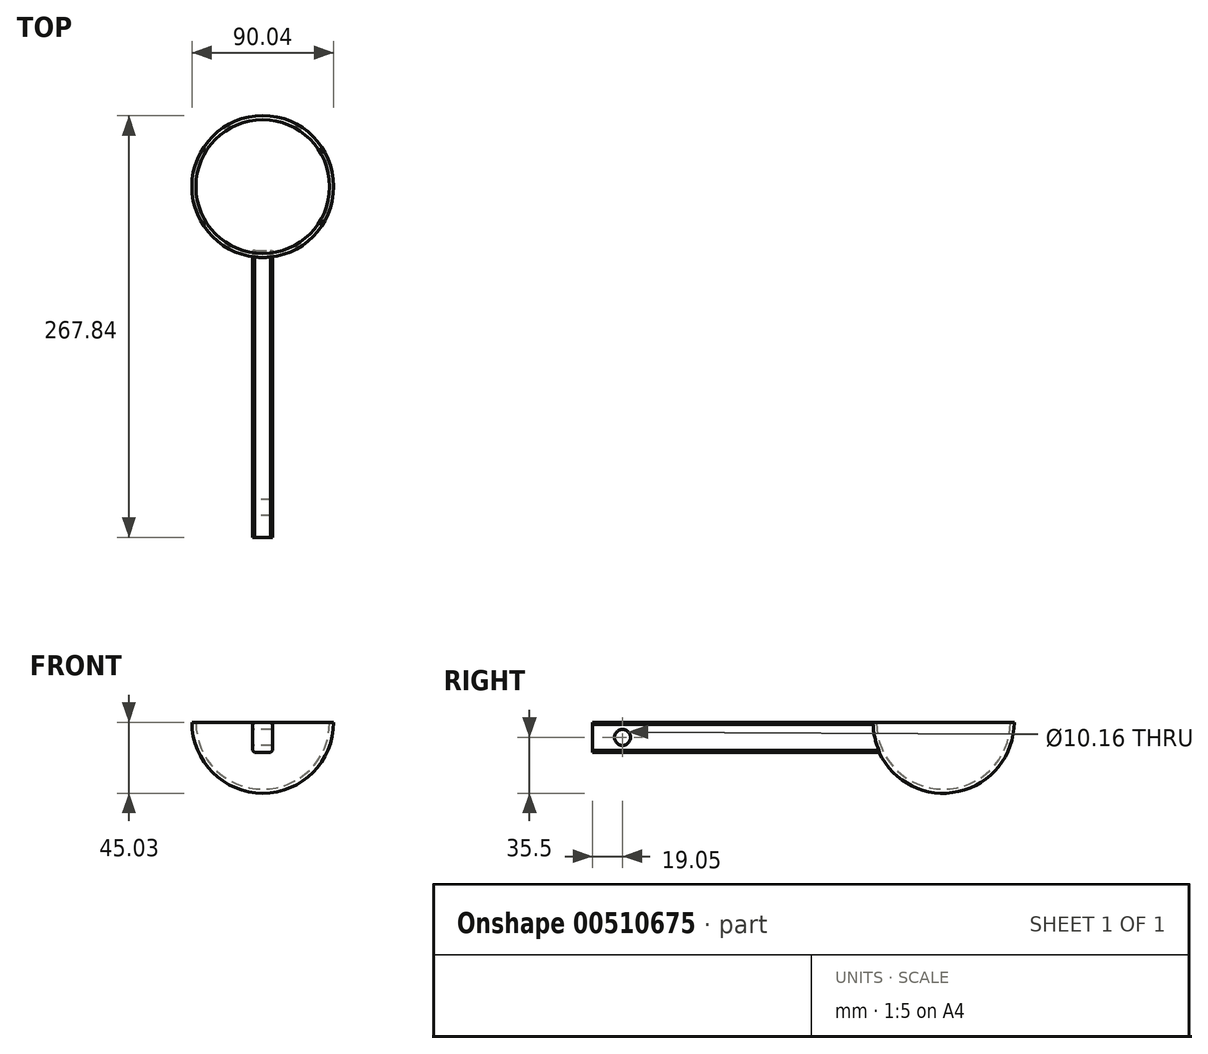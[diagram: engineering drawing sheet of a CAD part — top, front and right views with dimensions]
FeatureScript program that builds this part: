
annotation { "Feature Type Name" : "Feature", "Feature Type Description" : "" }
export const myFeature = defineFeature(function(context is Context, id is Id, definition is map)
    precondition{}
    {
        {
            var Q0;
            Q0=qCreatedBy(makeId("Right.planeOp"),FACE);
            var sketch = newSketch(context, id + "F0", { "sketchPlane" : qUnion([Q0])});
            skLineSegment(sketch, "E0.bottom", {"start": v(76.2, 9.53) * mm, "end": v(-76.2, 9.53) * mm});
            skLineSegment(sketch, "E0.right", {"start": v(-76.2, 9.53) * mm, "end": v(-76.2, -9.53) * mm});
            skPoint(sketch, "E0.middle", {"position": v(0, 0) * mm});
            skLineSegment(sketch, "E1", {"start": v(76.2, 9.53) * mm, "end": v(166.24, 9.53) * mm});
            skArc(sketch, "E2.MirrorCS", {"start": v(166.24, 9.53) * mm, "mid": v(121.22, -35.5) * mm, "end": v(76.2, 9.53) * mm});
            skLineSegment(sketch, "E3", {"start": v(-76.2, -9.53) * mm, "end": v(80.43, -9.53) * mm});
            skSolve(sketch);
        }
        {
            var Q0;
            {var subQ0=sQuery(id+"F0.wireOp",EDGE,"E0.bottom");Q0=makeQuery(id+"F0.imprint","IMPRINT",FACE,{"disambiguationData":[TD([[makeQuery(id+"F0.imprint","IMPRINT",EDGE,{"derivedFrom":subQ0}),1.0]])]});}
            extrude(context, id + "F1", {"entities" : qUnion([Q0]), "endBound" : BoundingType.SYMMETRIC, "depth" : 12.7 * mm});
        }
        {
            var Q0;
            {var subQ0=sQuery(id+"F0.wireOp",EDGE,"E1");Q0=makeQuery(id+"F0.imprint","IMPRINT",FACE,{"disambiguationData":[TD([[makeQuery(id+"F0.imprint","IMPRINT",EDGE,{"derivedFrom":subQ0}),-1.0]])]});}
            var Q1;
            Q1=sQuery(id+"F0.wireOp",EDGE,"E1");
            revolve(context, id + "F2", {"entities" : qUnion([Q0]), "axis" : qUnion([Q1]), "revolveType" : RevolveType.FULL});
        }
        {
            var Q0;
            Q0=makeQuery(id+"F1.opExtrude","SWEPT_FACE",FACE,{"disambiguationData":[OSD([sQuery(id+"F0.wireOp",EDGE,"E0.right")])]});
            extrude(context, id + "F3", {"entities" : qUnion([Q0]), "operationType" : NewBodyOperationType.ADD, "depth" : 25.4 * mm});
        }
        {
            var Q0;
            Q0=makeQuery(id+"F3.opExtrude","CAP_FACE",FACE,{"disambiguationData":[OSD([sQuery(id+"F0.wireOp",EDGE,"E0.right")])],"isStart":false});
            var sketch = newSketch(context, id + "F4", { "sketchPlane" : qUnion([Q0])});
            skLineSegment(sketch, "E4.0.0", {"start": v(-6.35, 9.53) * mm, "end": v(-6.35, -9.52) * mm});
            skLineSegment(sketch, "E4.0.1", {"start": v(-6.35, -9.52) * mm, "end": v(6.35, -9.52) * mm});
            skLineSegment(sketch, "E4.0.2", {"start": v(6.35, -9.52) * mm, "end": v(6.35, 9.53) * mm});
            skLineSegment(sketch, "E4.0.3", {"start": v(6.35, 9.53) * mm, "end": v(-6.35, 9.53) * mm});
            skLineSegment(sketch, "E5", {"start": v(64.15, 9.53) * mm, "end": v(-69.29, 9.53) * mm});
            skLineSegment(sketch, "E6", {"start": v(-69.29, 9.53) * mm, "end": v(-69.29, 62.6) * mm});
            skLineSegment(sketch, "E7", {"start": v(-69.29, 62.6) * mm, "end": v(64.15, 62.6) * mm});
            skLineSegment(sketch, "E8", {"start": v(64.15, 62.6) * mm, "end": v(64.15, 9.53) * mm});
            skSolve(sketch);
        }
        {
            var Q0;
            {var subQ0=sQuery(id+"F4.wireOp",EDGE,"E6");Q0=makeQuery(id+"F4.imprint","IMPRINT",FACE,{"disambiguationData":[TD([[makeQuery(id+"F4.imprint","IMPRINT",EDGE,{"derivedFrom":subQ0}),-1.0]])]});}
            extrude(context, id + "F5", {"entities" : qUnion([Q0]), "operationType" : NewBodyOperationType.REMOVE, "endBound" : BoundingType.THROUGH_ALL, "oppositeDirection" : true, "depth" : 25.4 * mm});
        }
        {
            var Q0;
            Q0=makeQuery(id+"F5.boolean.opBoolean","COPY",FACE,{"derivedFrom":makeQuery(id+"F5.opExtrude","SWEPT_FACE",FACE,{"disambiguationData":[OSD([sQuery(id+"F4.wireOp",EDGE,"E5")])]})});
            shell(context, id + "F6", {"entities" : qUnion([Q0]), "thickness" : 2.54 * mm});
        }
        {
            var Q0;
            Q0=qCreatedBy(makeId("Front.planeOp"),FACE);
            cPlane(context, id + "F7", {"entities" : qUnion([Q0]), "cplaneType" : CPlaneType.OFFSET, "offset" : 101.6 * mm, "width" : 152.4 * mm, "height" : 152.4 * mm});
        }
        {
            var Q0;
            Q0=qCreatedBy(id+"F7.planeOp",FACE);
            var sketch = newSketch(context, id + "F8", { "sketchPlane" : qUnion([Q0])});
            skLineSegment(sketch, "E9.0", {"start": v(-6.35, 9.53) * mm, "end": v(-6.35, -9.53) * mm});
            skLineSegment(sketch, "E10.0", {"start": v(6.35, 9.53) * mm, "end": v(6.35, -9.53) * mm});
            skLineSegment(sketch, "E11.0", {"start": v(6.35, 9.53) * mm, "end": v(-6.35, 9.53) * mm});
            skLineSegment(sketch, "E12.0", {"start": v(6.35, -9.53) * mm, "end": v(-6.35, -9.53) * mm});
            skSolve(sketch);
        }
        {
            var Q0;
            Q0=qSketchRegion(id+"F8",true);
            var Q1;
            Q1=makeQuery(id+"F2.opRevolve","SWEPT_FACE",FACE,{"disambiguationData":[OSD([sQuery(id+"F0.wireOp",EDGE,"E2.MirrorCS")])]});
            extrude(context, id + "F9", {"entities" : qUnion([Q0]), "endBound" : BoundingType.UP_TO_SURFACE, "oppositeDirection" : true, "endBoundEntityFace" : qUnion([Q1]), "depth" : 25.4 * mm});
        }
        {
            var Q0;
            Q0=makeQuery(id+"F1.opExtrude","SWEPT_BODY",BODY,{"disambiguationData":[OSD([sQuery(id+"F0.wireOp",EDGE,"E0.bottom"),sQuery(id+"F0.wireOp",EDGE,"E0.right"),sQuery(id+"F0.wireOp",EDGE,"E2.MirrorCS"),sQuery(id+"F0.wireOp",EDGE,"E3")])]});
            deleteBodies(context, id + "F10", {"entities" : qUnion([Q0])});
        }
        {
            var Q0;
            Q0=makeQuery(id+"F9.opExtrude","SWEPT_EDGE",EDGE,{"disambiguationData":[OSD([sQuery(id+"F8.wireOp",EDGE,"E9.0"),sQuery(id+"F8.wireOp",EDGE,"E11.0")])]});
            var Q1;
            Q1=makeQuery(id+"F9.opExtrude","SWEPT_EDGE",EDGE,{"disambiguationData":[OSD([sQuery(id+"F8.wireOp",EDGE,"E10.0"),sQuery(id+"F8.wireOp",EDGE,"E11.0")])]});
            var Q2;
            Q2=makeQuery(id+"F9.opExtrude","SWEPT_EDGE",EDGE,{"disambiguationData":[OSD([sQuery(id+"F8.wireOp",EDGE,"E9.0"),sQuery(id+"F8.wireOp",EDGE,"E12.0")])]});
            var Q3;
            Q3=makeQuery(id+"F9.opExtrude","SWEPT_EDGE",EDGE,{"disambiguationData":[OSD([sQuery(id+"F8.wireOp",EDGE,"E10.0"),sQuery(id+"F8.wireOp",EDGE,"E12.0")])]});
            chamfer(context, id + "F11", {"entities" : qUnion([Q0, Q1, Q2, Q3]), "width" : 1.27 * mm, "tangentPropagation" : true});
        }
        {
            var Q0;
            Q0=makeQuery(id+"F9.opExtrude","SWEPT_FACE",FACE,{"disambiguationData":[OSD([sQuery(id+"F8.wireOp",EDGE,"E9.0")])]});
            var sketch = newSketch(context, id + "F12", { "sketchPlane" : qUnion([Q0])});
            skCircle(sketch, "E13", {"center": v(82.55, 0) * mm, "radius": 5.08 * mm});
            skSolve(sketch);
        }
        {
            var Q0;
            Q0=qSketchRegion(id+"F12",true);
            extrude(context, id + "F13", {"entities" : qUnion([Q0]), "operationType" : NewBodyOperationType.REMOVE, "oppositeDirection" : true, "depth" : 25.4 * mm});
        }
    });
